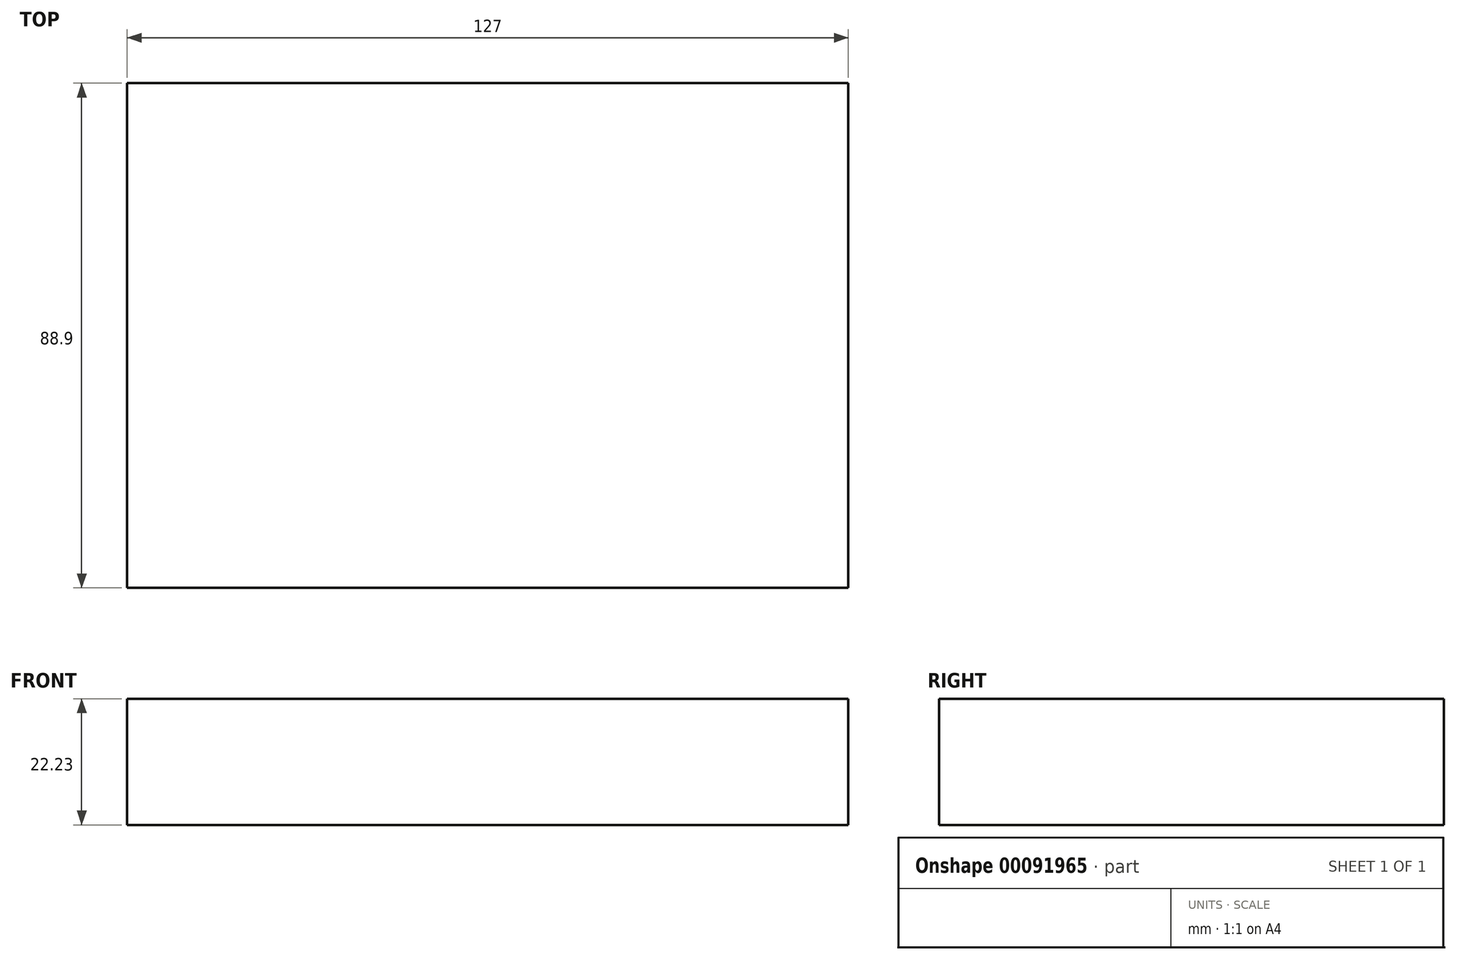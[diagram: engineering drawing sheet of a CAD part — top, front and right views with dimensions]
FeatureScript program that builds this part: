
annotation { "Feature Type Name" : "Feature", "Feature Type Description" : "" }
export const myFeature = defineFeature(function(context is Context, id is Id, definition is map)
    precondition{}
    {
        {
            var Q0;
            Q0=qCreatedBy(makeId("Top.planeOp"),FACE);
            var sketch = newSketch(context, id + "F0", { "sketchPlane" : qUnion([Q0])});
            skLineSegment(sketch, "E0.bottom", {"start": v(-63.5, -44.45) * mm, "end": v(63.5, -44.45) * mm});
            skLineSegment(sketch, "E0.top", {"start": v(-63.5, 44.45) * mm, "end": v(63.5, 44.45) * mm});
            skLineSegment(sketch, "E0.left", {"start": v(-63.5, -44.45) * mm, "end": v(-63.5, 44.45) * mm});
            skLineSegment(sketch, "E0.right", {"start": v(63.5, -44.45) * mm, "end": v(63.5, 44.45) * mm});
            skPoint(sketch, "E0.middle", {"position": v(0, 0) * mm});
            skSolve(sketch);
        }
        {
            var Q0;
            Q0=makeQuery(id+"F0.imprint","IMPRINT",FACE,{"disambiguationData":[TD([[makeQuery(id+"F0.imprint","IMPRINT",EDGE,{"derivedFrom":sQuery(id+"F0.wireOp",EDGE,"E0.bottom")}),1.0]])]});
            extrude(context, id + "F1", {"entities" : qUnion([Q0]), "depth" : 22.22 * mm});
        }
    });
